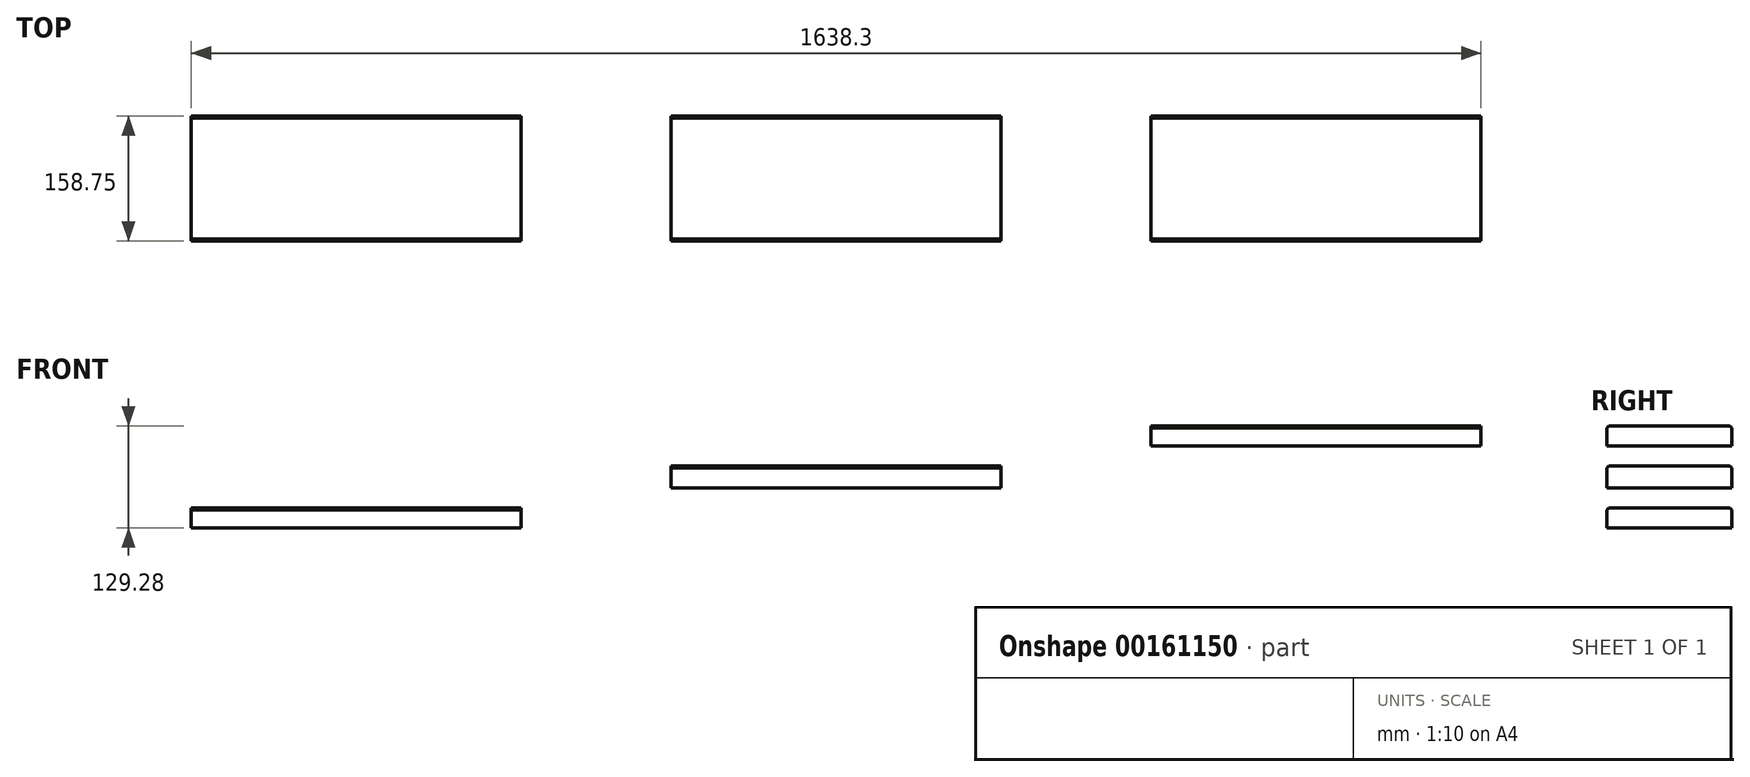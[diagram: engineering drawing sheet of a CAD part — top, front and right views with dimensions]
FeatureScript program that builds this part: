
annotation { "Feature Type Name" : "Feature", "Feature Type Description" : "" }
export const myFeature = defineFeature(function(context is Context, id is Id, definition is map)
    precondition{}
    {
        {
            var Q0;
            Q0=qCreatedBy(makeId("Front.planeOp"),FACE);
            var sketch = newSketch(context, id + "F0", { "sketchPlane" : qUnion([Q0])});
            skLineSegment(sketch, "E0.bottom", {"start": v(0, 0) * mm, "end": v(419.1, 0) * mm});
            skLineSegment(sketch, "E0.top", {"start": v(0, 25.4) * mm, "end": v(419.1, 25.4) * mm});
            skLineSegment(sketch, "E0.left", {"start": v(0, 0) * mm, "end": v(0, 25.4) * mm});
            skLineSegment(sketch, "E0.right", {"start": v(419.1, 0) * mm, "end": v(419.1, 25.4) * mm});
            skLineSegment(sketch, "E1.bottom", {"start": v(609.6, 78.48) * mm, "end": v(1028.7, 78.48) * mm});
            skLineSegment(sketch, "E1.top", {"start": v(609.6, 50.8) * mm, "end": v(1028.7, 50.8) * mm});
            skLineSegment(sketch, "E1.left", {"start": v(609.6, 78.48) * mm, "end": v(609.6, 50.8) * mm});
            skLineSegment(sketch, "E1.right", {"start": v(1028.7, 78.48) * mm, "end": v(1028.7, 50.8) * mm});
            skLineSegment(sketch, "E2.bottom", {"start": v(1219.2, 129.28) * mm, "end": v(1638.3, 129.28) * mm});
            skLineSegment(sketch, "E2.top", {"start": v(1219.2, 103.88) * mm, "end": v(1638.3, 103.88) * mm});
            skLineSegment(sketch, "E2.left", {"start": v(1219.2, 129.28) * mm, "end": v(1219.2, 103.88) * mm});
            skLineSegment(sketch, "E2.right", {"start": v(1638.3, 129.28) * mm, "end": v(1638.3, 103.88) * mm});
            skSolve(sketch);
        }
        {
            var Q0;
            Q0=qSketchRegion(id+"F0",true);
            extrude(context, id + "F1", {"entities" : qUnion([Q0]), "depth" : 158.75 * mm});
        }
        {
            var Q0;
            Q0=makeQuery(id+"F1.opExtrude","CAP_EDGE",EDGE,{"disambiguationData":[OSD([sQuery(id+"F0.wireOp",EDGE,"E0.top")])],"isStart":false});
            var Q1;
            Q1=makeQuery(id+"F1.opExtrude","CAP_EDGE",EDGE,{"disambiguationData":[OSD([sQuery(id+"F0.wireOp",EDGE,"E1.bottom")])],"isStart":false});
            var Q2;
            Q2=makeQuery(id+"F1.opExtrude","CAP_EDGE",EDGE,{"disambiguationData":[OSD([sQuery(id+"F0.wireOp",EDGE,"E2.bottom")])],"isStart":false});
            var Q3;
            Q3=makeQuery(id+"F1.opExtrude","CAP_EDGE",EDGE,{"disambiguationData":[OSD([sQuery(id+"F0.wireOp",EDGE,"E2.bottom")])],"isStart":true});
            var Q4;
            Q4=makeQuery(id+"F1.opExtrude","CAP_EDGE",EDGE,{"disambiguationData":[OSD([sQuery(id+"F0.wireOp",EDGE,"E1.bottom")])],"isStart":true});
            var Q5;
            Q5=makeQuery(id+"F1.opExtrude","CAP_EDGE",EDGE,{"disambiguationData":[OSD([sQuery(id+"F0.wireOp",EDGE,"E0.top")])],"isStart":true});
            chamfer(context, id + "F2", {"entities" : qUnion([Q0, Q1, Q2, Q3, Q4, Q5]), "width" : 2.54 * mm, "tangentPropagation" : true});
        }
    });
